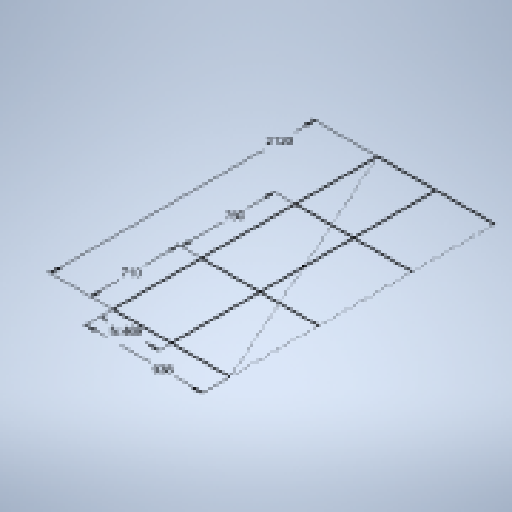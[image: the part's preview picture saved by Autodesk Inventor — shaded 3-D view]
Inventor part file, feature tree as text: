
AUTODESK INVENTOR PART (.ipt)
format: ipt  version: 2025 (Build 290162010, 162A)  size: 137,216 bytes
history: native  units: in
note: dims shown in document units (in); Inventor stores cm internally (conversion verified against a paired STEP export)
features: sketch x1
ambient origin geometry x8: Origin, YZ Plane, XZ Plane, XY Plane, X Axis, Y Axis, Z Axis, Center Point
feature tree (1):
  sketch  "Sketch3"  dims[d7=36.9291in d8=49.2126in d24=18.4646in d25=83.4646in d26=27.9528in d29=29.5276in]
